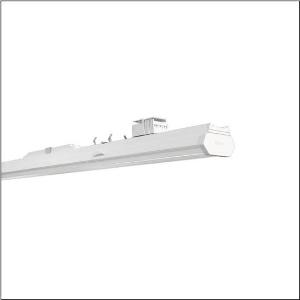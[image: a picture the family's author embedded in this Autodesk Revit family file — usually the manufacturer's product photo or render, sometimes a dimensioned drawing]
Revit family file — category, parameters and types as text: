
# Revit family: licross_11_protected_extreme_mo_51tp12dn495ge
name_source: partatom
category: Lighting Fixtures
units: mm (PartAtom-declared; Revit-internal decimal feet)

## family parameters
Cut with Voids When Loaded = No
Host = Face
Light Source = No
Part Type = Normal
Room Calculation Point = No
Round Connector Dimension = Use Diameter
Shared = No

## types (1)
- --- (1 x LED, 9980 lm, 57.1 W, 4000K)
    Apparent Load = 57 VA
    CIE Flux Codes = 73 92 98 99 100
    Color Rendering = 80
    Color Temperature = 4000K
    Default Elevation = 1800 mm
    Description = Licross 11 Protected extreme MO, luminaire insert, of sheet steel, galvanised, coil coated, white, length: 1.500mm, width: 90mm, height: 101mm, LED rated luminous flux: 9.980lm, light colour: 840, SDCM (Standard Deviation of Colour Matching)MacAdam ≤ 2 SDCM (initial), control gear: DALI 2, with plug, 5-pole, with phase selection, mains connection: 220..240V, AC, 50/60Hz, rated input power: 57W, internal wiring halogen-free, primary optical cover: cover, of PMMA, light emission: direct distribution, primary light characteristic: symmetric, protection rating (complete): IP64, insulation class (complete): insulation class I (protective earthing), certification: CE, ENEC, VDE, UKCA, protection symbol: D if used in an environment with conductive dust loads with corresponding accessories, impact resistance: IK06, permissible ambient temperature for indoor applications: -40..+45°C, corresponds to IFS (International Featured Standards) requirements for safety and quality in the food industry, reducing of maximum allowable ambient temperature of 5°C with ceiling mounting, LABS conformity tested according to VDMA 24364:2018-05, The light source and the operating device comply with the requirements of the Ecodesign Regulation (EU) 2019/2020 and are replaceable in accordance with this regulation, packaging unit: 1 piece
    Height = 92 mm
    Lamp = 1 x LED
    Lamp Light Flux = 9980 lm
    Lamp Power = 57.1 W
    Lamp count = 1
    Length = 1500 mm
    Luminous efficacy = 175 lm/W
    Manufacturer = Siteco
    ModVariant = No
    Model = 51TP12DN495GE
    Mounting Place = Ceiling
    Mounting Type = Pendant
    Number of Poles = 1
    OnlyDefault = Yes
    Power Factor = 1
    Product Name = Licross 11 Protected extreme MO
    Product group = luminaire insert | ceiling pendant
    ProductGroupID = 901
    Protection Class = Protection class I
    Protection Degree = IP 64
    RLX_Detail_Level = 1
    RLX_Emergency_Light_Flux = 0 lm
    RLX_Emergency_Type = 0
    RLX_Emergency_Type_DB = No
    RlxData = <blob elided: 24717 chars, md5=62ecaa2c>
    Socket = socket
    Standby Power = 0 W
    System Light Flux = 9980 lm
    System Power = 57 W
    Type Comments = factory setting: luminous flux: 100 % | dim-lin: 254 | 378 mA
    Type Image = l_1256148.jpg
    URL = http://relux.com
    VarID = @adj_089259
    Voltage = 0 V
    Weight = 0.00 kg
    Width = 88 mm

## geometry (parser evidence)
native form markers: Blend x4, Sweep x10
no freeform markers — native parametric forms only
